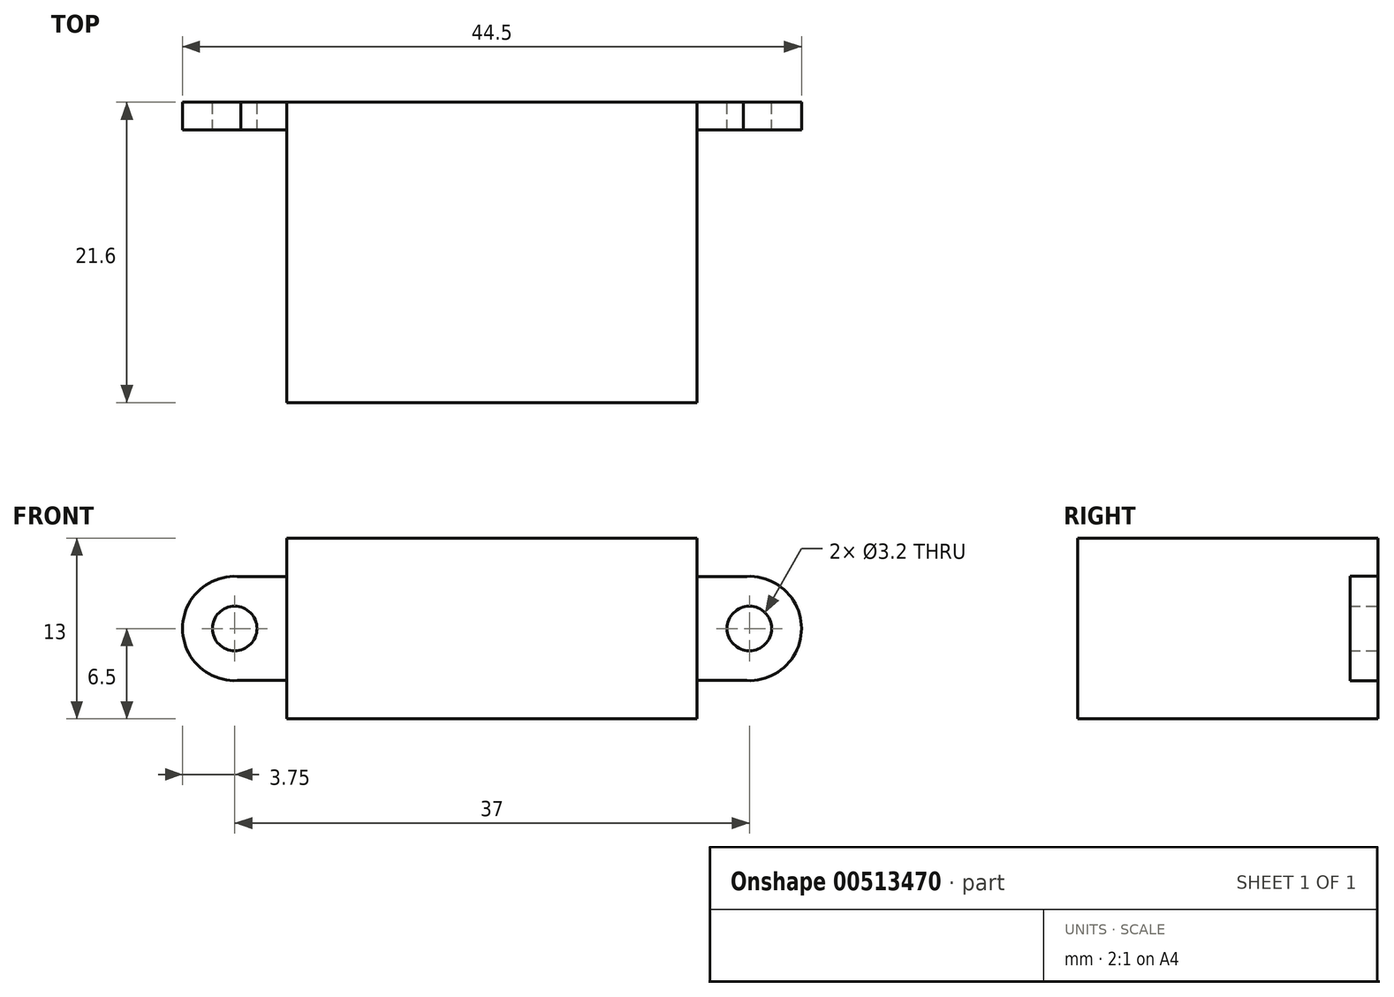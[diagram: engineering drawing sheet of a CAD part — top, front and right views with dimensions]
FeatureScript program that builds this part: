
annotation { "Feature Type Name" : "Feature", "Feature Type Description" : "" }
export const myFeature = defineFeature(function(context is Context, id is Id, definition is map)
    precondition{}
    {
        {
            var Q0;
            Q0=qCreatedBy(makeId("Front.planeOp"),FACE);
            var sketch = newSketch(context, id + "F0", { "sketchPlane" : qUnion([Q0])});
            skLineSegment(sketch, "E0.bottom", {"start": v(14.75, 6.5) * mm, "end": v(-14.75, 6.5) * mm});
            skLineSegment(sketch, "E0.top", {"start": v(14.75, -6.5) * mm, "end": v(-14.75, -6.5) * mm});
            skLineSegment(sketch, "E0.left", {"start": v(14.75, 6.5) * mm, "end": v(14.75, -6.5) * mm});
            skLineSegment(sketch, "E0.right", {"start": v(-14.75, 6.5) * mm, "end": v(-14.75, -6.5) * mm});
            skPoint(sketch, "E0.middle", {"position": v(0, 0) * mm});
            skSolve(sketch);
        }
        {
            var Q0;
            Q0 = qSketchRegion(id + "F0", true);
            extrude(context, id + "F1", {"entities" : qUnion([Q0]), "depth" : 21.6 * mm});
        }
        {
            var Q0;
            Q0=qCreatedBy(makeId("Front.planeOp"),FACE);
            var sketch = newSketch(context, id + "F2", { "sketchPlane" : qUnion([Q0])});
            skCircle(sketch, "E1", {"center": v(18.5, 0) * mm, "radius": 1.6 * mm});
            skArc(sketch, "E2", {"start": v(18.05, -3.72) * mm, "mid": v(22.25, 0) * mm, "end": v(18.05, 3.72) * mm});
            skLineSegment(sketch, "E3.bottom", {"start": v(18.95, 3.72) * mm, "end": v(0, 3.72) * mm});
            skLineSegment(sketch, "E3.top", {"start": v(18.95, -3.72) * mm, "end": v(0, -3.72) * mm});
            skPoint(sketch, "E3.middle", {"position": v(0, 0) * mm});
            skLineSegment(sketch, "E4", {"start": v(0, 3.72) * mm, "end": v(0, -3.72) * mm});
            skCircle(sketch, "E5.MirrorC", {"center": v(-18.5, 0) * mm, "radius": 1.6 * mm});
            skLineSegment(sketch, "E6.MirrorCS", {"start": v(-18.95, 3.72) * mm, "end": v(0, 3.72) * mm});
            skLineSegment(sketch, "E7.MirrorCS", {"start": v(-18.95, -3.72) * mm, "end": v(0, -3.72) * mm});
            skArc(sketch, "E8.MirrorCS", {"start": v(-18.05, -3.72) * mm, "mid": v(-22.25, 0) * mm, "end": v(-18.05, 3.72) * mm});
            skSolve(sketch);
        }
        {
            var Q0;
            Q0 = qSketchRegion(id + "F2", true);
            extrude(context, id + "F3", {"entities" : qUnion([Q0]), "operationType" : NewBodyOperationType.ADD, "depth" : 2 * mm});
        }
    });
